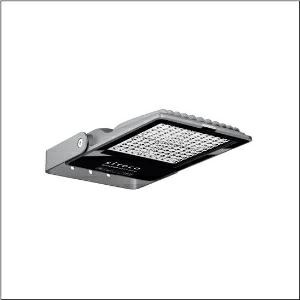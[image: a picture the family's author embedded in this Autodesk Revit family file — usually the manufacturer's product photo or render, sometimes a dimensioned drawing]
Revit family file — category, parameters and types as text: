
# Revit family: sicompact_r__31_mini___pl32_5xa7571f2k23_7a3f
name_source: partatom
category: Lighting Fixtures
units: mm (PartAtom-declared; Revit-internal decimal feet)

## family parameters
Cut with Voids When Loaded = No
Host = Face
Light Source = No
Part Type = Normal
Room Calculation Point = No
Round Connector Dimension = Use Diameter
Shared = No

## types (1)
- SiCompact® 31 mini  PL32 (1 x LED, 20000 lm, 130 W, 4000K)
    Apparent Load = 130 VA
    CIE Flux Codes = 32 69 98 100 100
    Color Rendering = 70
    Color Temperature = 4000K
    Default Elevation = 1800 mm
    Description = SiCompact® 31 mini, floodlight, primary light control with lens, of plastic, of toughened safety glass, transparent, light distribution: PL32, light emission: direct distribution, primary light characteristic: asymmetric, installation type: surface-mounted, LED, High Power LED, rated luminous flux: 20.000lm, luminous efficacy: 154lm/W, light colour: 740, colour temperature: 4000K, control gear: ECG, with cable, 3x 1.5mm², mains connection: 220..240V, AC, 50/60Hz, connection cable pre-assembled, cable length: 2m, rated input power: 130W, of diecast aluminium, specular, metallic grey (RAL 9006), length: 461mm, width: 261mm, height: 62mm, bracket, of sheet steel, coated, metallic grey (RAL 9006), ON/OFF, protection rating (complete): IP66, insulation class (complete): insulation class I (protective earthing), certification: CE, ENEC, impact resistance: IK08, permissible operating ambient temperature: -40..+45°C, packaging unit: 1 piece

Light Distribution: PL32
    Height = 62 mm  [stored 0.203412 ft]
    Lamp = 1 x LED
    Lamp Light Flux = 20000 lm
    Lamp Power = 130 W
    Lamp count = 1
    Length = 460 mm
    Luminous efficacy = 154 lm/W
    Manufacturer = Siteco
    ModVariant = No
    Model = 5XA7571F2K23
    Mounting Place = Wall
    Mounting Type = Surface mounted
    Number of Poles = 1
    OnlyDefault = Yes
    Power Factor = 1
    Product Name = SiCompact® 31 mini | PL32
    Product group = floodlight | wall mounted
    ProductGroupID = 2001
    Protection Class = Protection class I
    Protection Degree = IP 66
    RLX_Detail_Level = 1
    RLX_Emergency_Light_Flux = 0 lm
    RLX_Emergency_Type = 0
    RLX_Emergency_Type_DB = No
    RlxData = <blob elided: 126565 chars, md5=1bdeec3d>
    Socket = socket
    Standby Power = 0 W
    System Light Flux = 20000 lm
    System Power = 130 W
    Type Comments = Product without accessories
    Type Image = l_1006951.jpg
    URL = http://relux.com
    VarID = ---
    Voltage = 0 V
    Weight = 0.00 kg
    Width = 260 mm

note: [stored X ft] marks values corroborated as IEEE doubles in the binary element streams (Revit-internal decimal feet)

## geometry (parser evidence)
native form markers: Blend x4, Sweep x12
no freeform markers — native parametric forms only
